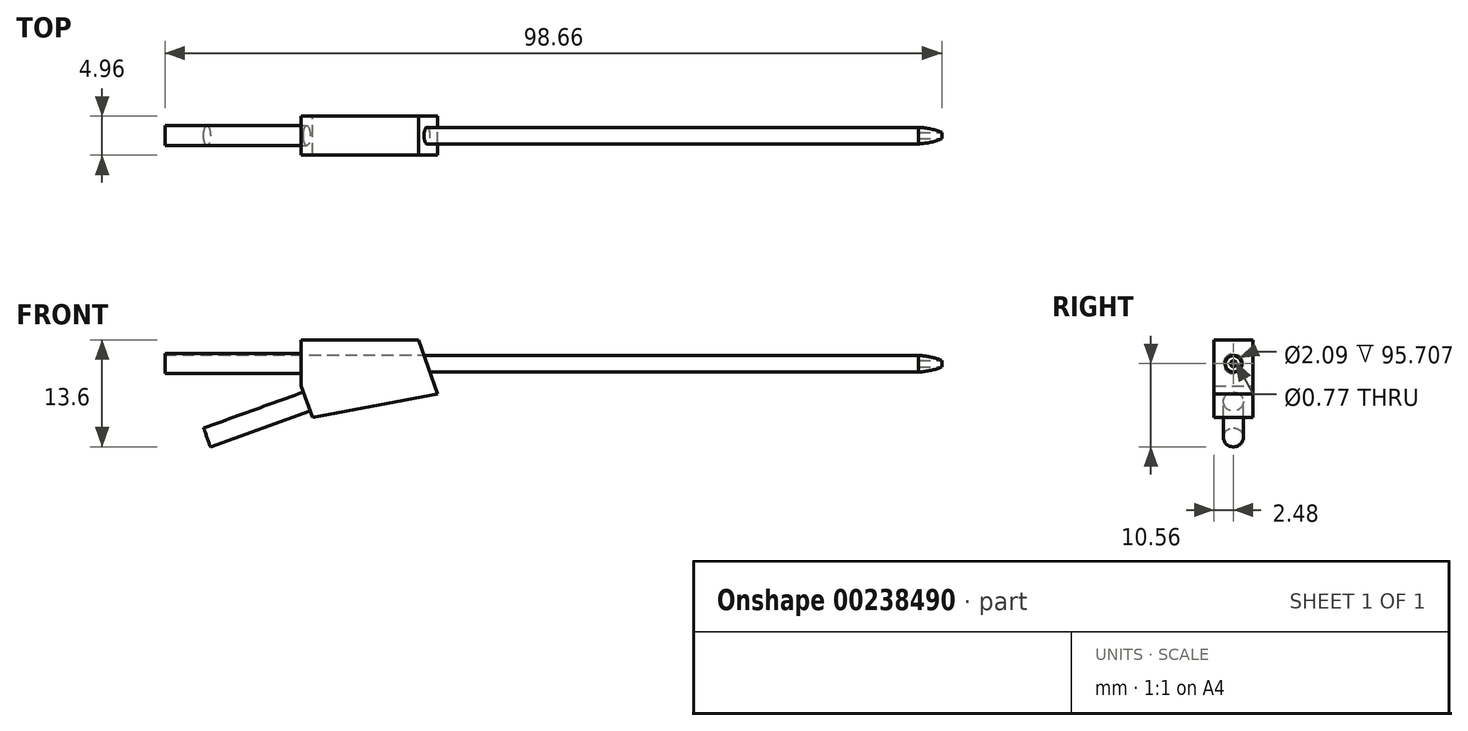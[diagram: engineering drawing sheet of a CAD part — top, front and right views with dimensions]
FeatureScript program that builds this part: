
annotation { "Feature Type Name" : "Feature", "Feature Type Description" : "" }
export const myFeature = defineFeature(function(context is Context, id is Id, definition is map)
    precondition{}
    {
        {
            var Q0;
            Q0=qCreatedBy(makeId("Front.planeOp"),FACE);
            var sketch = newSketch(context, id + "F0", { "sketchPlane" : qUnion([Q0])});
            skLineSegment(sketch, "E0.left", {"start": v(0, 1.05) * mm, "end": v(0, 0) * mm});
            skLineSegment(sketch, "E1", {"start": v(0, 1.05) * mm, "end": v(63.5, 1.05) * mm});
            skLineSegment(sketch, "E2", {"start": v(0, 0) * mm, "end": v(66.8, 0) * mm});
            skFitSpline(sketch, "E3", {"points": [v(63.5, 1.05) * mm, v(66.8, 0) * mm], "startDerivative": vector(2.57, -0.04) * mm, "endDerivative": vector(0.05, -1.8) * mm});
            skSolve(sketch);
        }
        {
            var Q0;
            Q0=makeQuery(id+"F0.imprint","IMPRINT",FACE,{"disambiguationData":[TD([[makeQuery(id+"F0.imprint","IMPRINT",EDGE,{"derivedFrom":sQuery(id+"F0.wireOp",EDGE,"E0.left")}),1.0]])]});
            var Q1;
            Q1=sQuery(id+"F0.wireOp",EDGE,"E2");
            revolve(context, id + "F1", {"entities" : qUnion([Q0]), "axis" : qUnion([Q1]), "revolveType" : RevolveType.FULL});
        }
        {
            var Q0;
            Q0=qCreatedBy(makeId("Front.planeOp"),FACE);
            var sketch = newSketch(context, id + "F2", { "sketchPlane" : qUnion([Q0])});
            skLineSegment(sketch, "E4", {"start": v(-14.93, 3.04) * mm, "end": v(-14.93, -2.8) * mm});
            skLineSegment(sketch, "E5", {"start": v(-14.93, -2.8) * mm, "end": v(-13.49, -6.82) * mm});
            skLineSegment(sketch, "E6", {"start": v(-13.49, -6.82) * mm, "end": v(2.4, -3.84) * mm});
            skLineSegment(sketch, "E7", {"start": v(2.4, -3.84) * mm, "end": v(0, 3.04) * mm});
            skLineSegment(sketch, "E8", {"start": v(-14.93, 3.04) * mm, "end": v(0, 3.04) * mm});
            skSolve(sketch);
        }
        {
            var Q0;
            Q0 = qSketchRegion(id + "F2", true);
            extrude(context, id + "F3", {"entities" : qUnion([Q0]), "operationType" : NewBodyOperationType.ADD, "depth" : 4.95 * mm, "symmetric" : true});
        }
        {
            var Q0;
            Q0=makeQuery(id+"F3.opExtrude","SWEPT_FACE",FACE,{"disambiguationData":[OSD([sQuery(id+"F2.wireOp",EDGE,"E4")])]});
            var sketch = newSketch(context, id + "F4", { "sketchPlane" : qUnion([Q0])});
            skCircle(sketch, "E9", {"center": v(0, 0) * mm, "radius": 1.27 * mm});
            skSolve(sketch);
        }
        {
            var Q0;
            Q0 = qSketchRegion(id + "F4", true);
            extrude(context, id + "F5", {"entities" : qUnion([Q0]), "operationType" : NewBodyOperationType.ADD, "depth" : 17.27 * mm});
        }
        {
            var Q0;
            Q0=makeQuery(id+"F3.opExtrude","SWEPT_FACE",FACE,{"disambiguationData":[OSD([sQuery(id+"F2.wireOp",EDGE,"E5")])]});
            var sketch = newSketch(context, id + "F6", { "sketchPlane" : qUnion([Q0])});
            skCircle(sketch, "E10", {"center": v(0, 0.29) * mm, "radius": 1.27 * mm});
            skPoint(sketch, "E11.start.orphan", {"position": v(-2.48, 0.29) * mm});
            skPoint(sketch, "E12.trimOffspring.end.orphan", {"position": v(0, -1.85) * mm});
            skPoint(sketch, "E13.trimOffspring.end.orphan", {"position": v(2.48, 0.29) * mm});
            skPoint(sketch, "E14.start.orphan", {"position": v(0, 2.42) * mm});
            skSolve(sketch);
        }
        {
            var Q0;
            Q0 = qSketchRegion(id + "F6", true);
            extrude(context, id + "F7", {"entities" : qUnion([Q0]), "operationType" : NewBodyOperationType.ADD, "depth" : 13.46 * mm});
        }
        {
            var Q0;
            Q0=makeQuery(id+"F5.opExtrude","CAP_FACE",FACE,{"disambiguationData":[OSD([sQuery(id+"F4.wireOp",EDGE,"E9")])],"isStart":false});
            var sketch = newSketch(context, id + "F8", { "sketchPlane" : qUnion([Q0])});
            skCircle(sketch, "E15", {"center": v(0, 0) * mm, "radius": 1.04 * mm});
            skSolve(sketch);
        }
        {
            var Q0;
            Q0 = qSketchRegion(id + "F8", true);
            extrude(context, id + "F9", {"entities" : qUnion([Q0]), "operationType" : NewBodyOperationType.REMOVE, "oppositeDirection" : true, "depth" : 95.7 * mm, "offsetDistance" : 25.4 * mm, "hasSecondDirection" : true, "secondDirectionBound" : BoundingType.THROUGH_ALL, "secondDirectionOppositeDirection" : false, "secondDirectionDepth" : 27.94 * mm});
        }
        {
            var Q0;
            Q0=qCreatedBy(makeId("Right.planeOp"),FACE);
            var sketch = newSketch(context, id + "F10", { "sketchPlane" : qUnion([Q0])});
            skCircle(sketch, "E16", {"center": v(0, 0) * mm, "radius": 0.38 * mm});
            skSolve(sketch);
        }
        {
            var Q0;
            Q0 = qSketchRegion(id + "F10", true);
            extrude(context, id + "F11", {"entities" : qUnion([Q0]), "operationType" : NewBodyOperationType.REMOVE, "endBound" : BoundingType.THROUGH_ALL, "oppositeDirection" : true, "depth" : 25.4 * mm, "offsetDistance" : 25.4 * mm, "hasSecondDirection" : true, "secondDirectionBound" : BoundingType.THROUGH_ALL, "secondDirectionOppositeDirection" : false, "secondDirectionDepth" : 25.4 * mm});
        }
    });
